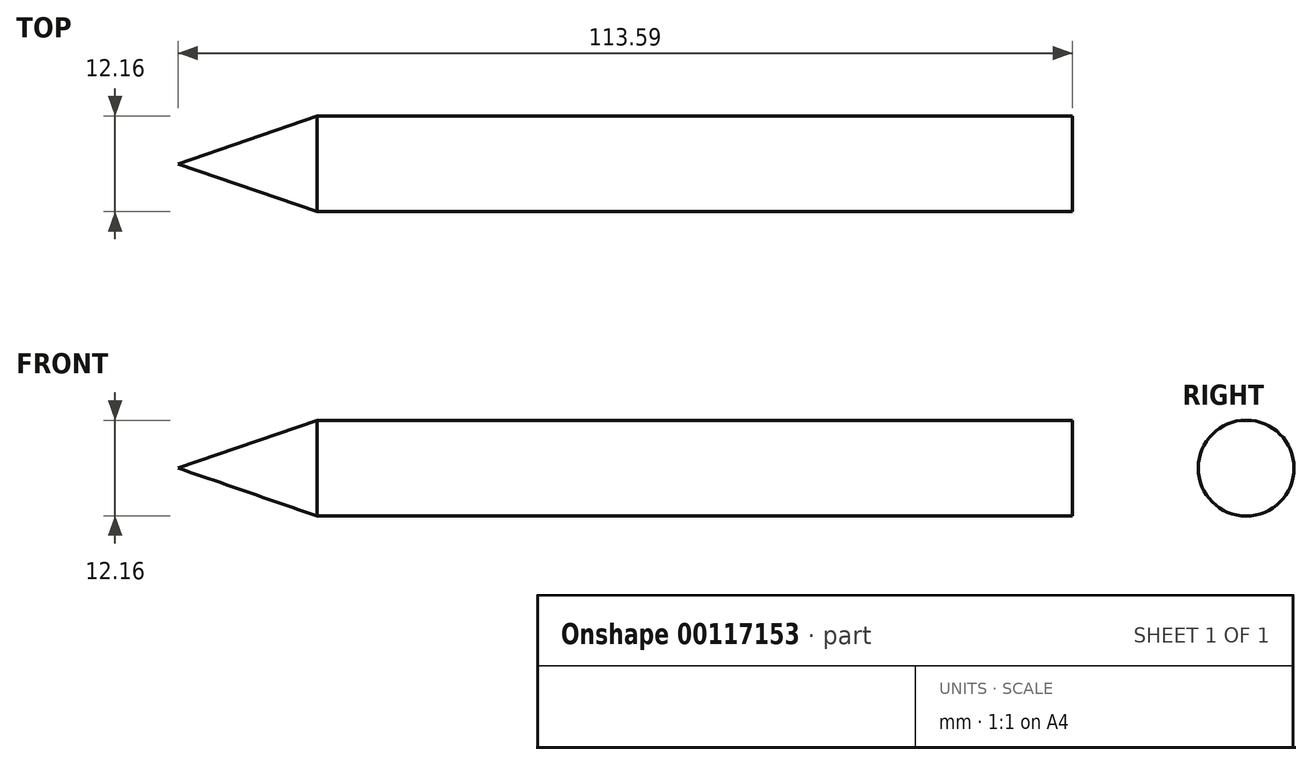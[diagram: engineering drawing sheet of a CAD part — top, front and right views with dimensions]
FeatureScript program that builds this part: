
annotation { "Feature Type Name" : "Feature", "Feature Type Description" : "" }
export const myFeature = defineFeature(function(context is Context, id is Id, definition is map)
    precondition{}
    {
        {
            var Q0;
            Q0=qCreatedBy(makeId("Front.planeOp"),FACE);
            var sketch = newSketch(context, id + "F0", { "sketchPlane" : qUnion([Q0])});
            skLineSegment(sketch, "E0.bottom", {"start": v(-47.98, 0) * mm, "end": v(47.98, 0) * mm});
            skLineSegment(sketch, "E0.top", {"start": v(-47.98, 6.08) * mm, "end": v(47.98, 6.08) * mm});
            skLineSegment(sketch, "E0.left", {"start": v(-47.98, 0) * mm, "end": v(-47.98, 6.08) * mm});
            skLineSegment(sketch, "E0.right", {"start": v(47.98, 0) * mm, "end": v(47.98, 6.08) * mm});
            skPoint(sketch, "E0.middle", {"position": v(0, 3.04) * mm});
            skLineSegment(sketch, "E1", {"start": v(-47.98, 0) * mm, "end": v(-65.61, 0) * mm});
            skLineSegment(sketch, "E2", {"start": v(-65.61, 0) * mm, "end": v(-47.98, 6.08) * mm});
            skSolve(sketch);
        }
        {
            var Q0;
            Q0=makeQuery(id+"F0.imprint","IMPRINT",FACE,{"disambiguationData":[TD([[makeQuery(id+"F0.imprint","IMPRINT",EDGE,{"derivedFrom":sQuery(id+"F0.wireOp",EDGE,"E0.bottom")}),1.0]])]});
            var Q1;
            Q1=sQuery(id+"F0.wireOp",EDGE,"E0.bottom");
            revolve(context, id + "F1", {"entities" : qUnion([Q0]), "axis" : qUnion([Q1]), "revolveType" : RevolveType.FULL});
        }
        {
            var Q0;
            Q0=makeQuery(id+"F0.imprint","IMPRINT",FACE,{"disambiguationData":[TD([[makeQuery(id+"F0.imprint","IMPRINT",EDGE,{"derivedFrom":sQuery(id+"F0.wireOp",EDGE,"E0.left")}),1.0]])]});
            var Q1;
            Q1=sQuery(id+"F0.wireOp",EDGE,"E1");
            revolve(context, id + "F2", {"operationType" : NewBodyOperationType.ADD, "entities" : qUnion([Q0]), "axis" : qUnion([Q1]), "revolveType" : RevolveType.FULL});
        }
    });
